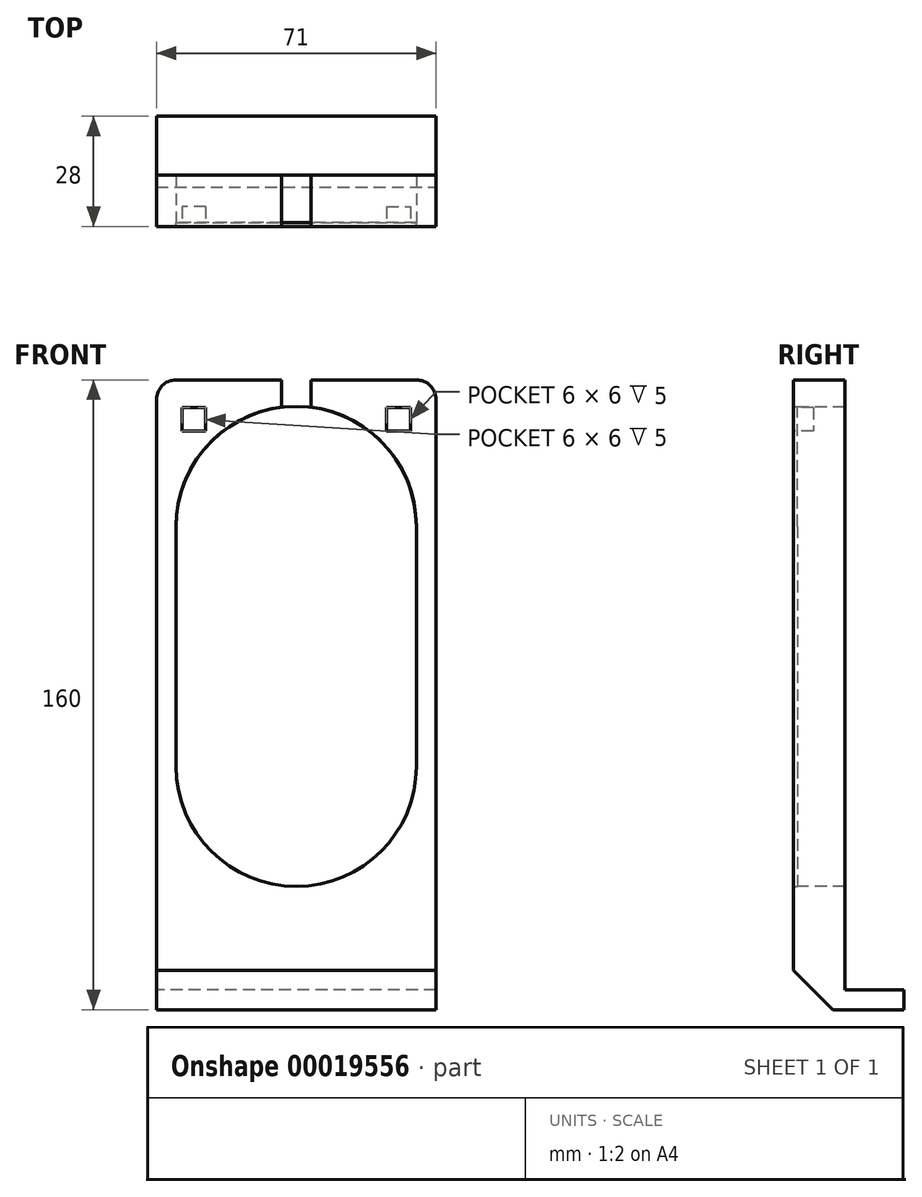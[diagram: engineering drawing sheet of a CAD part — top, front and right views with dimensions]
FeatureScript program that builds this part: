
annotation { "Feature Type Name" : "Feature", "Feature Type Description" : "" }
export const myFeature = defineFeature(function(context is Context, id is Id, definition is map)
    precondition{}
    {
        {
            var Q0;
            Q0=qCreatedBy(makeId("Front.planeOp"),FACE);
            var sketch = newSketch(context, id + "F0", { "sketchPlane" : qUnion([Q0])});
            skArc(sketch, "E0", {"start": v(30.5, 38.8) * mm, "mid": v(0, 69.3) * mm, "end": v(-30.5, 38.8) * mm});
            skArc(sketch, "E1", {"start": v(-30.5, -22.2) * mm, "mid": v(0, -52.7) * mm, "end": v(30.5, -22.2) * mm});
            skLineSegment(sketch, "E2", {"start": v(-30.5, 38.8) * mm, "end": v(-30.5, -22.2) * mm});
            skLineSegment(sketch, "E3", {"start": v(30.5, 38.8) * mm, "end": v(30.5, -22.2) * mm});
            skSolve(sketch);
        }
        {
            var Q0;
            Q0=makeQuery(id+"F0.imprint","IMPRINT",FACE,{"disambiguationData":[TD([[makeQuery(id+"F0.imprint","IMPRINT",EDGE,{"derivedFrom":sQuery(id+"F0.wireOp",EDGE,"E0")}),1.0]])]});
            extrude(context, id + "F1", {"entities" : qUnion([Q0]), "depth" : 1 * mm});
        }
        {
            var Q0;
            Q0=makeQuery(id+"F1.opExtrude","CAP_FACE",FACE,{"disambiguationData":[OSD([sQuery(id+"F0.wireOp",EDGE,"E0"),sQuery(id+"F0.wireOp",EDGE,"E1"),sQuery(id+"F0.wireOp",EDGE,"E2"),sQuery(id+"F0.wireOp",EDGE,"E3")])],"isStart":false});
            var sketch = newSketch(context, id + "F2", { "sketchPlane" : qUnion([Q0])});
            skLineSegment(sketch, "E4.1", {"start": v(35.5, 40.5) * mm, "end": v(35.5, -20.5) * mm});
            skLineSegment(sketch, "E4.3", {"start": v(-35.5, 40.5) * mm, "end": v(-35.5, -20.5) * mm});
            skArc(sketch, "E5", {"start": v(30.5, 38.8) * mm, "mid": v(22.85, 58.99) * mm, "end": v(3.75, 69.06) * mm});
            skArc(sketch, "E6", {"start": v(-30.5, -22.2) * mm, "mid": v(0, -52.7) * mm, "end": v(30.5, -22.2) * mm});
            skLineSegment(sketch, "E7", {"start": v(-30.5, -22.2) * mm, "end": v(-30.5, 38.8) * mm});
            skLineSegment(sketch, "E8", {"start": v(30.5, 38.8) * mm, "end": v(30.5, -22.2) * mm});
            skLineSegment(sketch, "E9", {"start": v(-3.75, 76) * mm, "end": v(-3.75, 69.06) * mm});
            skLineSegment(sketch, "E10", {"start": v(3.75, 76) * mm, "end": v(3.75, 69.06) * mm});
            skLineSegment(sketch, "E11", {"start": v(0, 76) * mm, "end": v(0, 38.8) * mm, "construction": true});
            skArc(sketch, "E12.trimOffspring", {"start": v(-3.75, 69.06) * mm, "mid": v(-22.85, 58.99) * mm, "end": v(-30.5, 38.8) * mm});
            skLineSegment(sketch, "E13", {"start": v(-30.5, 76) * mm, "end": v(-3.75, 76) * mm});
            skLineSegment(sketch, "E14", {"start": v(-35.5, 71) * mm, "end": v(-35.5, 40.5) * mm});
            skLineSegment(sketch, "E15", {"start": v(3.75, 76) * mm, "end": v(30.5, 76) * mm});
            skLineSegment(sketch, "E16", {"start": v(35.5, 71) * mm, "end": v(35.5, 40.5) * mm});
            skLineSegment(sketch, "E17", {"start": v(0, -79) * mm, "end": v(47.95, -79) * mm, "construction": true});
            skLineSegment(sketch, "E18", {"start": v(-35.5, -20.5) * mm, "end": v(-35.5, -79) * mm});
            skLineSegment(sketch, "E19", {"start": v(-35.5, -79) * mm, "end": v(-35.5, -84) * mm});
            skLineSegment(sketch, "E20", {"start": v(35.5, -20.5) * mm, "end": v(35.5, -79) * mm});
            skLineSegment(sketch, "E21", {"start": v(35.5, -79) * mm, "end": v(35.5, -84) * mm});
            skLineSegment(sketch, "E22", {"start": v(35.5, -84) * mm, "end": v(-35.5, -84) * mm});
            skPoint(sketch, "E23.visualSharp", {"position": v(35.5, 76) * mm});
            skArc(sketch, "E23.filletArc", {"start": v(35.5, 71) * mm, "mid": v(34.04, 74.54) * mm, "end": v(30.5, 76) * mm});
            skPoint(sketch, "E24.visualSharp", {"position": v(-35.5, 76) * mm});
            skArc(sketch, "E24.filletArc", {"start": v(-30.5, 76) * mm, "mid": v(-34.04, 74.54) * mm, "end": v(-35.5, 71) * mm});
            skSolve(sketch);
        }
        {
            var Q0;
            Q0 = qSketchRegion(id + "F2", true);
            extrude(context, id + "F3", {"entities" : qUnion([Q0]), "oppositeDirection" : true, "depth" : 13 * mm});
        }
        {
            var Q0;
            Q0=makeQuery(id+"F3.opExtrude","CAP_FACE",FACE,{"disambiguationData":[OSD([sQuery(id+"F2.wireOp",EDGE,"E4.1"),sQuery(id+"F2.wireOp",EDGE,"E4.3"),sQuery(id+"F2.wireOp",EDGE,"E5"),sQuery(id+"F2.wireOp",EDGE,"E6"),sQuery(id+"F2.wireOp",EDGE,"E7"),sQuery(id+"F2.wireOp",EDGE,"E8"),sQuery(id+"F2.wireOp",EDGE,"E9"),sQuery(id+"F2.wireOp",EDGE,"E10"),sQuery(id+"F2.wireOp",EDGE,"E12.trimOffspring"),sQuery(id+"F2.wireOp",EDGE,"E13"),sQuery(id+"F2.wireOp",EDGE,"E14"),sQuery(id+"F2.wireOp",EDGE,"E15"),sQuery(id+"F2.wireOp",EDGE,"E16"),sQuery(id+"F2.wireOp",EDGE,"E18"),sQuery(id+"F2.wireOp",EDGE,"E19"),sQuery(id+"F2.wireOp",EDGE,"E20"),sQuery(id+"F2.wireOp",EDGE,"E21"),sQuery(id+"F2.wireOp",EDGE,"E22")])],"isStart":false});
            var sketch = newSketch(context, id + "F4", { "sketchPlane" : qUnion([Q0])});
            skLineSegment(sketch, "E25.bottom", {"start": v(-35.5, -84) * mm, "end": v(35.5, -84) * mm});
            skLineSegment(sketch, "E25.top", {"start": v(-35.5, -79) * mm, "end": v(35.5, -79) * mm});
            skLineSegment(sketch, "E25.left", {"start": v(35.5, -84) * mm, "end": v(35.5, -79) * mm});
            skLineSegment(sketch, "E25.right", {"start": v(-35.5, -84) * mm, "end": v(-35.5, -79) * mm});
            skSolve(sketch);
        }
        {
            var Q0;
            Q0 = qSketchRegion(id + "F4", true);
            extrude(context, id + "F5", {"entities" : qUnion([Q0]), "operationType" : NewBodyOperationType.ADD, "depth" : 15 * mm});
        }
        {
            var Q0;
            Q0=makeQuery(id+"F3.opExtrude","CAP_FACE",FACE,{"disambiguationData":[OSD([sQuery(id+"F2.wireOp",EDGE,"E4.1"),sQuery(id+"F2.wireOp",EDGE,"E4.3"),sQuery(id+"F2.wireOp",EDGE,"E5"),sQuery(id+"F2.wireOp",EDGE,"E6"),sQuery(id+"F2.wireOp",EDGE,"E7"),sQuery(id+"F2.wireOp",EDGE,"E8"),sQuery(id+"F2.wireOp",EDGE,"E9"),sQuery(id+"F2.wireOp",EDGE,"E10"),sQuery(id+"F2.wireOp",EDGE,"E12.trimOffspring"),sQuery(id+"F2.wireOp",EDGE,"E13"),sQuery(id+"F2.wireOp",EDGE,"E14"),sQuery(id+"F2.wireOp",EDGE,"E15"),sQuery(id+"F2.wireOp",EDGE,"E16"),sQuery(id+"F2.wireOp",EDGE,"E18"),sQuery(id+"F2.wireOp",EDGE,"E19"),sQuery(id+"F2.wireOp",EDGE,"E20"),sQuery(id+"F2.wireOp",EDGE,"E21"),sQuery(id+"F2.wireOp",EDGE,"E22")])],"isStart":true});
            var sketch = newSketch(context, id + "F6", { "sketchPlane" : qUnion([Q0])});
            skLineSegment(sketch, "E26.rect.bottom", {"start": v(-23, 69) * mm, "end": v(-29, 69) * mm});
            skLineSegment(sketch, "E26.rect.top", {"start": v(-23, 63) * mm, "end": v(-29, 63) * mm});
            skLineSegment(sketch, "E26.rect.left", {"start": v(-23, 69) * mm, "end": v(-23, 63) * mm});
            skLineSegment(sketch, "E26.rect.right", {"start": v(-29, 69) * mm, "end": v(-29, 63) * mm});
            skPoint(sketch, "E26.rect.middle", {"position": v(-26, 66) * mm});
            skLineSegment(sketch, "E27.rect.bottom", {"start": v(23, 69) * mm, "end": v(29, 69) * mm});
            skLineSegment(sketch, "E27.rect.top", {"start": v(23, 63) * mm, "end": v(29, 63) * mm});
            skLineSegment(sketch, "E27.rect.left", {"start": v(23, 69) * mm, "end": v(23, 63) * mm});
            skLineSegment(sketch, "E27.rect.right", {"start": v(29, 69) * mm, "end": v(29, 63) * mm});
            skPoint(sketch, "E27.rect.middle", {"position": v(26, 66) * mm});
            skLineSegment(sketch, "E28", {"start": v(0, 68.28) * mm, "end": v(0, 53.4) * mm, "construction": true});
            skSolve(sketch);
        }
        {
            var Q0;
            Q0 = qSketchRegion(id + "F6", true);
            extrude(context, id + "F7", {"entities" : qUnion([Q0]), "operationType" : NewBodyOperationType.REMOVE, "oppositeDirection" : true, "depth" : 5 * mm});
        }
        {
            var Q0;
            Q0=makeQuery(id+"F5.boolean.opBoolean","MERGE",FACE,{"derivedFrom":[makeQuery(id+"F3.opExtrude","SWEPT_FACE",FACE,{"disambiguationData":[OSD([sQuery(id+"F2.wireOp",EDGE,"E4.1"),sQuery(id+"F2.wireOp",EDGE,"E16"),sQuery(id+"F2.wireOp",EDGE,"E20"),sQuery(id+"F2.wireOp",EDGE,"E21")])]}),makeQuery(id+"F5.opExtrude","SWEPT_FACE",FACE,{"disambiguationData":[OSD([sQuery(id+"F4.wireOp",EDGE,"E25.right")])]})]});
            var sketch = newSketch(context, id + "F8", { "sketchPlane" : qUnion([Q0])});
            skLineSegment(sketch, "E29", {"start": v(-1, -74) * mm, "end": v(9, -84) * mm});
            skLineSegment(sketch, "E30", {"start": v(9, -84) * mm, "end": v(-1, -84) * mm});
            skLineSegment(sketch, "E31", {"start": v(-1, -84) * mm, "end": v(-1, -74) * mm});
            skSolve(sketch);
        }
        {
            var Q0;
            Q0 = qSketchRegion(id + "F8", true);
            extrude(context, id + "F9", {"entities" : qUnion([Q0]), "operationType" : NewBodyOperationType.REMOVE, "endBound" : BoundingType.THROUGH_ALL, "oppositeDirection" : true, "depth" : 25 * mm, "offsetDistance" : 25 * mm});
        }
    });
